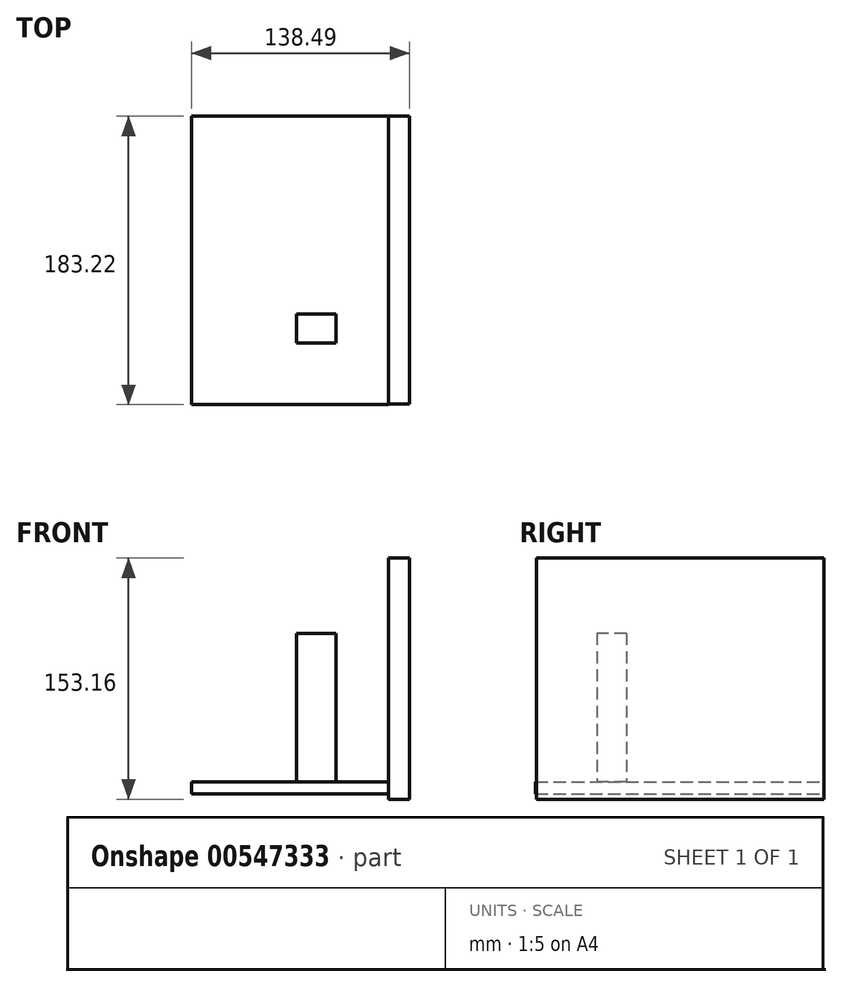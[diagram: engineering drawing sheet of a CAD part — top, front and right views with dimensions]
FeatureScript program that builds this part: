
annotation { "Feature Type Name" : "Feature", "Feature Type Description" : "" }
export const myFeature = defineFeature(function(context is Context, id is Id, definition is map)
    precondition{}
    {
        {
            var Q0;
            Q0=qCreatedBy(makeId("Top.planeOp"),FACE);
            var sketch = newSketch(context, id + "F0", { "sketchPlane" : qUnion([Q0])});
            skLineSegment(sketch, "E0.bottom", {"start": v(-11.73, 10.53) * mm, "end": v(13.23, 10.53) * mm});
            skLineSegment(sketch, "E0.top", {"start": v(-11.73, -8.12) * mm, "end": v(13.23, -8.12) * mm});
            skLineSegment(sketch, "E0.left", {"start": v(-11.73, 10.53) * mm, "end": v(-11.73, -8.12) * mm});
            skLineSegment(sketch, "E0.right", {"start": v(13.23, 10.53) * mm, "end": v(13.23, -8.12) * mm});
            skSolve(sketch);
        }
        {
            var Q0;
            Q0=makeQuery(id+"F0.imprint","IMPRINT",FACE,{"disambiguationData":[TD([[makeQuery(id+"F0.imprint","IMPRINT",EDGE,{"derivedFrom":sQuery(id+"F0.wireOp",EDGE,"E0.bottom")}),-1.0]])]});
            extrude(context, id + "F1", {"entities" : qUnion([Q0]), "depth" : 25.4 * mm, "offsetDistance" : 25.4 * mm});
        }
        {
            var Q0;
            Q0=makeQuery(id+"F1.opExtrude","CAP_FACE",FACE,{"disambiguationData":[OSD([sQuery(id+"F0.wireOp",EDGE,"E0.bottom"),sQuery(id+"F0.wireOp",EDGE,"E0.top"),sQuery(id+"F0.wireOp",EDGE,"E0.left"),sQuery(id+"F0.wireOp",EDGE,"E0.right")])],"isStart":true});
            var sketch = newSketch(context, id + "F2", { "sketchPlane" : qUnion([Q0])});
            skSolve(sketch);
        }
        {
            var Q0;
            Q0=makeQuery(id+"F2.imprint","IMPRINT",FACE,{"disambiguationData":[TD([[makeQuery(id+"F2.imprint","IMPRINT",EDGE,{"derivedFrom":makeQuery(id+"F1.opExtrude","CAP_EDGE",EDGE,{"disambiguationData":[OSD([sQuery(id+"F0.wireOp",EDGE,"E0.bottom")])],"isStart":true})}),1.0]])]});
            extrude(context, id + "F3", {"entities" : qUnion([Q0]), "operationType" : NewBodyOperationType.ADD, "depth" : 69.1 * mm, "offsetDistance" : 25.4 * mm});
        }
        {
            var Q0;
            Q0=makeQuery(id+"F3.opExtrude","CAP_FACE",FACE,{"disambiguationData":[OSD([sQuery(id+"F0.wireOp",EDGE,"E0.bottom"),sQuery(id+"F0.wireOp",EDGE,"E0.top"),sQuery(id+"F0.wireOp",EDGE,"E0.left"),sQuery(id+"F0.wireOp",EDGE,"E0.right")])],"isStart":false});
            var sketch = newSketch(context, id + "F4", { "sketchPlane" : qUnion([Q0])});
            skLineSegment(sketch, "E1.bottom", {"start": v(-78.53, 47.2) * mm, "end": v(46.64, 47.2) * mm});
            skLineSegment(sketch, "E1.top", {"start": v(-78.53, -136.02) * mm, "end": v(46.64, -136.02) * mm});
            skLineSegment(sketch, "E1.left", {"start": v(-78.53, 47.2) * mm, "end": v(-78.53, -136.02) * mm});
            skLineSegment(sketch, "E1.right", {"start": v(46.64, 47.2) * mm, "end": v(46.64, -136.02) * mm});
            skLineSegment(sketch, "E2.bottom", {"start": v(46.64, -136.02) * mm, "end": v(59.96, -136.02) * mm});
            skLineSegment(sketch, "E2.top", {"start": v(46.64, 46.73) * mm, "end": v(59.96, 46.73) * mm});
            skLineSegment(sketch, "E2.left", {"start": v(46.64, -136.02) * mm, "end": v(46.64, 46.73) * mm});
            skLineSegment(sketch, "E2.right", {"start": v(59.96, -136.02) * mm, "end": v(59.96, 46.73) * mm});
            skSolve(sketch);
        }
        {
            var Q0;
            Q0=makeQuery(id+"F4.imprint","IMPRINT",FACE,{"disambiguationData":[TD([[makeQuery(id+"F4.imprint","IMPRINT",EDGE,{"derivedFrom":makeQuery(id+"F3.opExtrude","CAP_EDGE",EDGE,{"disambiguationData":[OSD([sQuery(id+"F0.wireOp",EDGE,"E0.bottom")])],"isStart":false})}),1.0]])]});
            var Q1;
            Q1=makeQuery(id+"F4.imprint","IMPRINT",FACE,{"disambiguationData":[TD([[makeQuery(id+"F4.imprint","IMPRINT",EDGE,{"derivedFrom":sQuery(id+"F4.wireOp",EDGE,"E1.bottom")}),-1.0]])]});
            extrude(context, id + "F5", {"entities" : qUnion([Q0, Q1]), "operationType" : NewBodyOperationType.ADD, "depth" : 7.62 * mm, "offsetDistance" : 25.4 * mm});
        }
        {
            var Q0;
            Q0=makeQuery(id+"F4.imprint","IMPRINT",FACE,{"disambiguationData":[TD([[makeQuery(id+"F4.imprint","IMPRINT",EDGE,{"derivedFrom":sQuery(id+"F4.wireOp",EDGE,"E2.bottom")}),1.0]])]});
            extrude(context, id + "F6", {"entities" : qUnion([Q0]), "operationType" : NewBodyOperationType.ADD, "endBound" : BoundingType.SYMMETRIC, "oppositeDirection" : true, "depth" : 21.84 * mm, "offsetDistance" : 25.4 * mm});
        }
        {
            var Q0;
            Q0=makeQuery(id+"F6.opExtrude","CAP_FACE",FACE,{"disambiguationData":[OSD([sQuery(id+"F4.wireOp",EDGE,"E2.bottom"),sQuery(id+"F4.wireOp",EDGE,"E2.top"),sQuery(id+"F4.wireOp",EDGE,"E2.left"),sQuery(id+"F4.wireOp",EDGE,"E2.right")])],"isStart":false});
            extrude(context, id + "F7", {"entities" : qUnion([Q0]), "operationType" : NewBodyOperationType.ADD, "depth" : 131.32 * mm, "offsetDistance" : 25.4 * mm});
        }
    });
